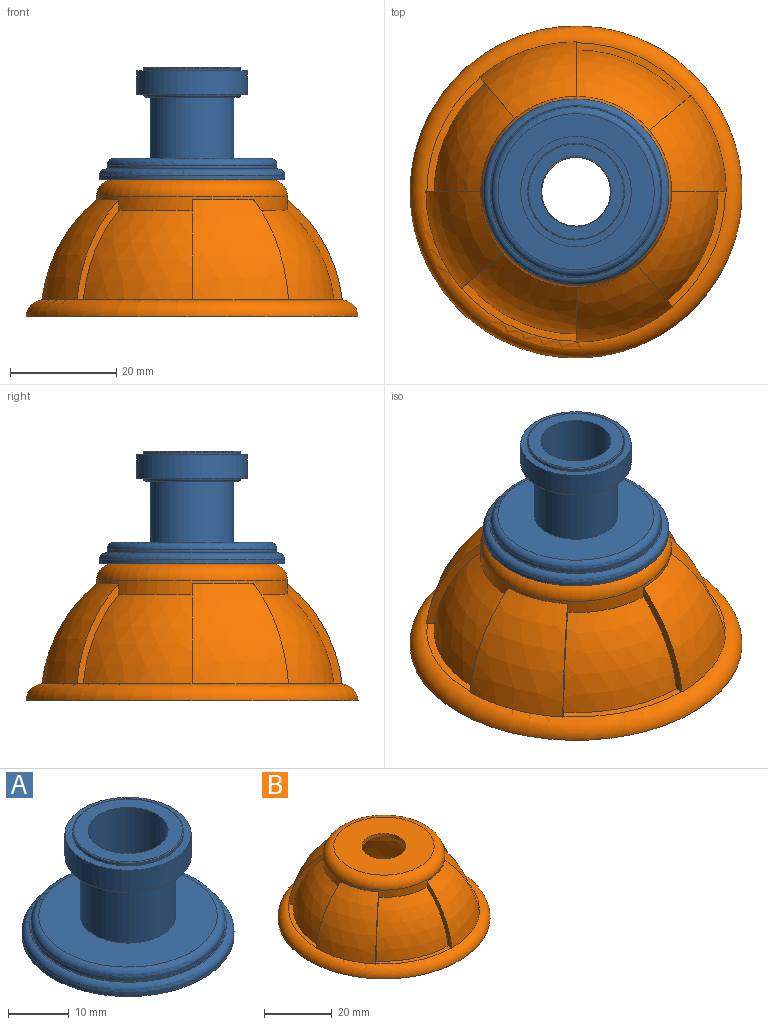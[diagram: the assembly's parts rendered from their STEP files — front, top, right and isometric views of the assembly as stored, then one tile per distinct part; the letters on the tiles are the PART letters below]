
ASSEMBLY  parts=2 mates=1
PART A: 17 faces, bbox 37.9x37.9x21.4 mm
  f0: cylinder r=6.6mm len=21.19mm, axis (0,0,1), area 879.3mm2, adj f1,f13
  f1: plane 17.94x17.94mm, normal (0,0,1), area 115.7mm2, adj f0,f2
  f2: torus R=8.97mm, axis (0,0,1), area 15.7mm2, adj f1,f3
  f3: cylinder r=9.14mm len=18.29mm, axis (0,0,1), area 29.2mm2, adj f2,f4
  f4: plane 20.83x20.83mm, normal (0,0,1), area 78mm2, adj f3,f5
  f5: cylinder r=10.41mm len=20.83mm, axis (0,0,1), area 294.4mm2, adj f4,f6
  f6: plane 20.83x20.83mm, normal (0,0,-1), area 78mm2, adj f5,f16
  f7: plane 17.27x17.27mm, normal (0,0,-1), area 39.5mm2, adj f8,f16
  f8: cylinder r=7.87mm len=15.75mm, axis (0,0,1), area 568.9mm2, adj f7,f9
  f9: plane 29.46x29.46mm, normal (0,0,1), area 486.9mm2, adj f8,f14
  f10: cylinder r=16mm len=32mm, axis (0,0,1), area 73.4mm2, adj f11,f14
  f11: plane 32.46x32.46mm, normal (0,0,1), area 23.3mm2, adj f10,f15
  f12: cylinder r=17.5mm len=35mm, axis (0,0,1), area 80.3mm2, adj f13,f15
  f13: plane 35x35mm, normal (0,0,-1), area 825.1mm2, adj f0,f12
  f14: torus R=14.73mm, axis (0,0,-1), area 194.8mm2, adj f9,f10
  f15: torus R=16.23mm, axis (0,0,-1), area 213.6mm2, adj f11,f12
  f16: torus R=8.64mm, axis (0,0,1), area 44.9mm2, adj f6,f7
PART B: 28 faces, bbox 67.8x67.8x28.1 mm
  f0: cylinder r=18.01mm len=36.02mm, axis (0,0,-1), area 195.3mm2, adj f1,f2,f3,f10,f11,f15,f16,f17
  f1: sphere r=26.98mm, area 398mm2, adj f0,f4,f19,f23
  f2: sphere r=26.98mm, area 398mm2, adj f0,f5,f18,f25
  f3: sphere r=26.98mm, area 398mm2, adj f0,f6,f16,f26
  f4: plane 21.56x10.93mm, normal (0,0,1), area 32.6mm2, adj f1,f7,f19,f23
  f5: plane 21.56x10.93mm, normal (0,0,1), area 32.6mm2, adj f2,f7,f18,f25
  f6: plane 21.56x10.93mm, normal (0,0,1), area 32.6mm2, adj f3,f7,f16,f26
  f7: torus R=28.15mm, axis (0,0,-1), area 931.8mm2, adj f4,f5,f6,f12,f13,f15,f16,f17
  f8: sphere r=25.45mm, area 3936.3mm2, adj f14,f27
  f9: plane 29.67x29.67mm, normal (0,0,1), area 559.4mm2, adj f10,f27
  f10: torus R=14.83mm, axis (0,0,-1), area 528.2mm2, adj f0,f9
  f11: sphere r=26.98mm, area 398mm2, adj f0,f12,f17,f22
  f12: plane 21.56x10.93mm, normal (0,0,1), area 32.6mm2, adj f7,f11,f17,f22
  f13: cylinder r=31.33mm len=62.65mm, axis (0,0,-1), area 0.6mm2, adj f7,f14
  f14: plane 62.65x62.65mm, normal (0,0,-1), area 1047.6mm2, adj f8,f13
  f15: sphere r=28.5mm, area 376.4mm2, adj f0,f7,f16,f17
  f16: plane 18.92x7.9mm, normal (0.64,-0.77,0), area 31.7mm2, adj f0,f3,f6,f7,f15
  f17: plane 18.92x10.31mm, normal (0,1,0), area 31.7mm2, adj f0,f7,f11,f12,f15
  f18: plane 18.92x10.31mm, normal (0,-1,0), area 31.7mm2, adj f0,f2,f5,f7,f20
  f19: plane 18.92x7.9mm, normal (-0.64,0.77,0), area 31.7mm2, adj f0,f1,f4,f7,f20
  f20: sphere r=28.5mm, area 376.4mm2, adj f0,f7,f18,f19
  f21: sphere r=28.5mm, area 376.4mm2, adj f0,f7,f22,f23
  f22: plane 18.92x7.9mm, normal (-0.77,-0.64,0), area 31.7mm2, adj f0,f7,f11,f12,f21
  f23: plane 18.92x10.31mm, normal (1,0,0), area 31.7mm2, adj f0,f1,f4,f7,f21
  f24: sphere r=28.5mm, area 376.4mm2, adj f0,f7,f25,f26
  f25: plane 18.92x7.9mm, normal (0.77,0.64,0), area 31.7mm2, adj f0,f2,f5,f7,f24
  f26: plane 18.92x10.31mm, normal (-1,0,0), area 31.7mm2, adj f0,f3,f6,f7,f24
  f27: cylinder r=6.48mm len=12.95mm, axis (0,0,1), area 51.4mm2, adj f8,f9
PLACE A t=(0.36,1.19,10.25)mm
PLACE B t=(0.36,1.19,-15.63)mm
MATE fastened B.f0 <-> A.f0  axis (0,0,1) through (0.36,1.19,10.25)mm
